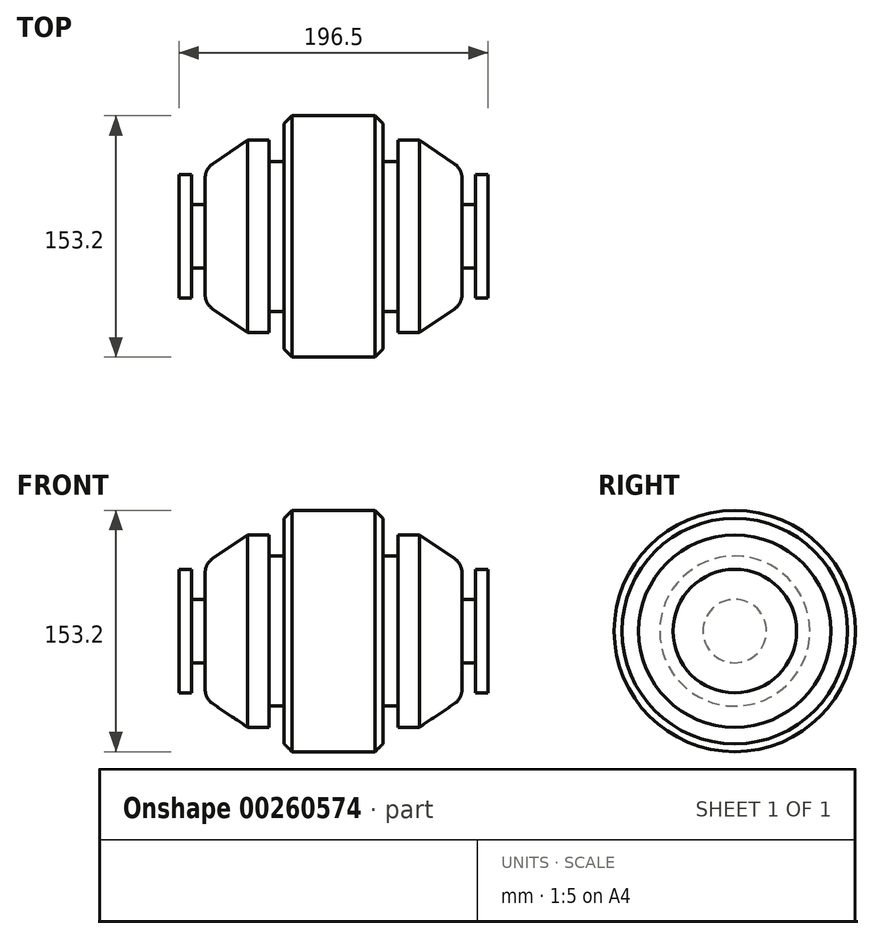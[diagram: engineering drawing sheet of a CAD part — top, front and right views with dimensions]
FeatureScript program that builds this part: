
annotation { "Feature Type Name" : "Feature", "Feature Type Description" : "" }
export const myFeature = defineFeature(function(context is Context, id is Id, definition is map)
    precondition{}
    {
        {
            var Q0;
            Q0=qCreatedBy(makeId("Front.planeOp"),FACE);
            var sketch = newSketch(context, id + "F0", { "sketchPlane" : qUnion([Q0])});
            skLineSegment(sketch, "E0", {"start": v(0, 0) * mm, "end": v(-98.25, 0) * mm});
            skLineSegment(sketch, "E1", {"start": v(-98.25, 0) * mm, "end": v(-98.25, 39.27) * mm});
            skLineSegment(sketch, "E2", {"start": v(-98.25, 39.27) * mm, "end": v(-90.18, 39.27) * mm});
            skLineSegment(sketch, "E3", {"start": v(-90.18, 39.27) * mm, "end": v(-90.18, 20.16) * mm});
            skLineSegment(sketch, "E4", {"start": v(-90.18, 20.16) * mm, "end": v(-81.52, 20.16) * mm});
            skLineSegment(sketch, "E5", {"start": v(-81.52, 20.16) * mm, "end": v(-81.52, 42.85) * mm});
            skLineSegment(sketch, "E6", {"start": v(-81.52, 42.85) * mm, "end": v(-54.65, 61.07) * mm});
            skLineSegment(sketch, "E7", {"start": v(-54.65, 61.07) * mm, "end": v(-40.91, 61.07) * mm});
            skLineSegment(sketch, "E8", {"start": v(-40.91, 61.07) * mm, "end": v(-40.91, 47.63) * mm});
            skLineSegment(sketch, "E9", {"start": v(-40.91, 47.63) * mm, "end": v(-31.36, 47.63) * mm});
            skLineSegment(sketch, "E10", {"start": v(-31.36, 47.63) * mm, "end": v(-31.36, 76.6) * mm});
            skLineSegment(sketch, "E11", {"start": v(-31.36, 76.6) * mm, "end": v(0, 76.6) * mm});
            skLineSegment(sketch, "E12", {"start": v(0, 76.6) * mm, "end": v(0, 0) * mm});
            skSolve(sketch);
        }
        {
            var Q0;
            Q0=makeQuery(id+"F0.imprint","IMPRINT",FACE,{"disambiguationData":[TD([[makeQuery(id+"F0.imprint","IMPRINT",EDGE,{"derivedFrom":sQuery(id+"F0.wireOp",EDGE,"E0")}),-1.0]])]});
            var Q1;
            Q1=sQuery(id+"F0.wireOp",EDGE,"E0");
            revolve(context, id + "F1", {"entities" : qUnion([Q0]), "axis" : qUnion([Q1]), "revolveType" : RevolveType.FULL});
        }
        {
            var Q0;
            Q0=makeQuery(id+"F1.opRevolve","SWEPT_EDGE",EDGE,{"disambiguationData":[OSD([sQuery(id+"F0.wireOp",EDGE,"E5"),sQuery(id+"F0.wireOp",EDGE,"E6")])]});
            fillet(context, id + "F2", {"entities" : qUnion([Q0]), "radius" : 10.6 * mm, "tangentPropagation" : true, "allowEdgeOverflow" : false});
        }
        {
            var Q0;
            Q0=makeQuery(id+"F1.opRevolve","SWEPT_EDGE",EDGE,{"disambiguationData":[OSD([sQuery(id+"F0.wireOp",EDGE,"E10"),sQuery(id+"F0.wireOp",EDGE,"E11")])]});
            chamfer(context, id + "F3", {"entities" : qUnion([Q0]), "width" : 5 * mm, "tangentPropagation" : true});
        }
        {
            var Q0;
            Q0=makeQuery(id+"F1.opRevolve","SWEPT_BODY",BODY,{"disambiguationData":[OSD([sQuery(id+"F0.wireOp",EDGE,"E0"),sQuery(id+"F0.wireOp",EDGE,"E1"),sQuery(id+"F0.wireOp",EDGE,"E2"),sQuery(id+"F0.wireOp",EDGE,"E3"),sQuery(id+"F0.wireOp",EDGE,"E4"),sQuery(id+"F0.wireOp",EDGE,"E5"),sQuery(id+"F0.wireOp",EDGE,"E6"),sQuery(id+"F0.wireOp",EDGE,"E7"),sQuery(id+"F0.wireOp",EDGE,"E8"),sQuery(id+"F0.wireOp",EDGE,"E9"),sQuery(id+"F0.wireOp",EDGE,"E10"),sQuery(id+"F0.wireOp",EDGE,"E11"),sQuery(id+"F0.wireOp",EDGE,"E12")])]});
            var Q1;
            Q1=makeQuery(id+"F1.opRevolve","SWEPT_FACE",FACE,{"disambiguationData":[OSD([sQuery(id+"F0.wireOp",EDGE,"E12")])]});
            mirror(context, id + "F4", {"operationType" : NewBodyOperationType.ADD, "entities" : qUnion([Q0]), "mirrorPlane" : qUnion([Q1])});
        }
        {
            var Q0;
            Q0=makeQuery(id+"F1.opRevolve","SWEPT_BODY",BODY,{"disambiguationData":[OSD([sQuery(id+"F0.wireOp",EDGE,"E0"),sQuery(id+"F0.wireOp",EDGE,"E1"),sQuery(id+"F0.wireOp",EDGE,"E2"),sQuery(id+"F0.wireOp",EDGE,"E3"),sQuery(id+"F0.wireOp",EDGE,"E4"),sQuery(id+"F0.wireOp",EDGE,"E5"),sQuery(id+"F0.wireOp",EDGE,"E6"),sQuery(id+"F0.wireOp",EDGE,"E7"),sQuery(id+"F0.wireOp",EDGE,"E8"),sQuery(id+"F0.wireOp",EDGE,"E9"),sQuery(id+"F0.wireOp",EDGE,"E10"),sQuery(id+"F0.wireOp",EDGE,"E11"),sQuery(id+"F0.wireOp",EDGE,"E12")])]});
            var Q1;
            Q1=qCreatedBy(makeId("Right.planeOp"),FACE);
            mirror(context, id + "F5", {"operationType" : NewBodyOperationType.ADD, "entities" : qUnion([Q0]), "mirrorPlane" : qUnion([Q1])});
        }
    });
